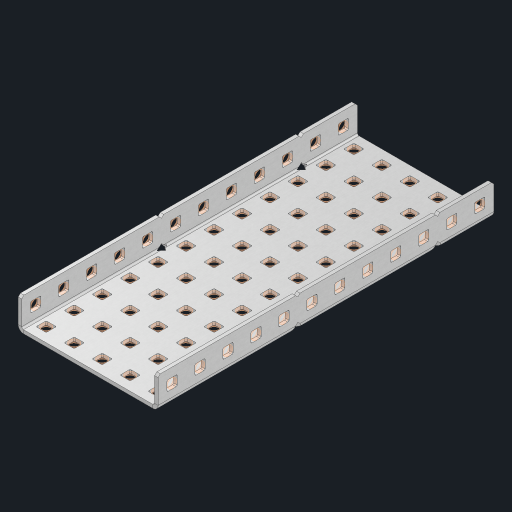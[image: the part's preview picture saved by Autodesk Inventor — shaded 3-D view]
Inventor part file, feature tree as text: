
AUTODESK INVENTOR PART (.ipt)
format: ipt  version: 2023 (Build 270158000, 158)  size: 1,160,192 bytes
history: native  units: in
note: dims shown in document units (in); Inventor stores cm internally (conversion verified against a paired STEP export)
features: other x89, extrude x83, sheet_metal_op x10, sketch x8, mirror x1, pattern_linear x1, chamfer x1
ambient origin geometry x8: Origin, YZ Plane, XZ Plane, XY Plane, X Axis, Y Axis, Z Axis, Center Point
bodies: Solid1 (feature_tree), Body (feature_tree)
feature tree (193):
  other  "Flange Pattern Plane"
  sheet_metal_op  "Flange Pattern"
  sheet_metal_op  "Body Pattern"
  other  "Arc Length"
  mirror  "Notch Mirror"
  pattern_linear  "Notch Pattern"  Spacing1=0.25in  [1 undecoded]
  chamfer  "End Chamfer"
  extrude  "Half Cut"  Depth=0.0625in
  sketch  "Sketch1"  dims[d0=2.5in]
  other  "Plate1"
  sketch  "Sketch2"  dims[d1=6.0in]
  other  "Plate2"
  sheet_metal_op  "Bend1"
  sheet_metal_op  "Corner1"
  sketch  "Sketch3"  dims[d2=0.0625in]
  other  "Flange Pattern Sketch"
  sketch  "Sketch7"  dims[d3=0.0625in]
  other  "Srf1"
  other  "Srf2"
  sketch  "Sketch8"  dims[d4=0.0312in]
  sketch  "Sketch9"  dims[d5=0.125in]
  other  "Srf91"
  sheet_metal_op  "Body Pattern Sketch"
  other  "Srf92"
  sketch  "Sketch13"  dims[d6=0.0625in]
  sketch  "Sketch14"  dims[d7=0.5in d8=90.0deg d9=0.0312in d10=0.25in d11=0.0625in d12=0.0625in d16=0.182in d17=0.02in d18=0.0625in d19=0.0in d20=0.25in d21=0.25in d46=0.172in d47=1.0in d48=0.0in d49=0.182in d50=0.02in d51=0.25in d52=0.25in d53=0.0625in d54=0.0in d55=0.172in d56=1.0in d57=0.0in d60=4.7244in d62=0.5in d63=1.9685in d65=0.5in d85=0.1473in d86=0.1782in d88=0.04in d89=0.0625in d90=0.0in d91=0.04in d92=0.0491in d95=2.5in d96=0.04in d97=0.25in d98=45.0deg d101=0.0in d102=2.497in d131=2.5in d132=4.7244in d134=0.5in d139=0.5in]
  other  "Srf856"
  other  "Srf1310"
  other  "Srf1311"
  other  "Srf1312"
  other  "Srf1376"
  other  "Srf1377"
  other  "Srf1728"
  other  "Srf1755"
  other  "Srf1878"
  other  "Srf1879"
  other  "Srf1880"
  other  "Srf1881"
  other  "Srf1882"
  other  "Srf1883"
  other  "Srf1884"
  other  "Srf1885"
  other  "Srf1886"
  other  "Srf1887"
  other  "Srf1888"
  other  "Srf1889"
  other  "Srf1890"
  other  "Srf1891"
  other  "Srf1892"
  other  "Srf1893"
  other  "Srf1894"
  other  "Srf1895"
  other  "Srf1942"
  other  "Srf1943"
  other  "Srf1944"
  other  "Srf1945"
  other  "Srf1946"
  other  "Srf1947"
  other  "Srf1948"
  other  "Srf1949"
  other  "Srf1950"
  other  "Srf1951"
  other  "Srf1952"
  other  "Srf1953"
  other  "Srf1954"
  other  "Srf1955"
  other  "Srf1956"
  other  "Srf1957"
  other  "Srf1958"
  other  "Srf1959"
  other  "Srf1960"
  other  "Srf1961"
  other  "Srf1962"
  other  "Srf1963"
  other  "Srf1964"
  other  "Srf1965"
  other  "Srf1966"
  other  "Srf1967"
  other  "Srf1968"
  other  "Srf1969"
  other  "Srf1970"
  other  "Srf2146"
  other  "Srf2147"
  other  "Srf2148"
  other  "Srf2149"
  other  "Srf2150"
  other  "Srf2151"
  other  "Srf2152"
  other  "Srf2153"
  other  "Srf2154"
  other  "Srf2155"
  other  "Srf2156"
  other  "Srf2157"
  other  "Srf2158"
  other  "Srf2159"
  other  "Srf2160"
  other  "Srf2161"
  other  "Srf2162"
  other  "Srf2163"
  other  "Srf2164"
  other  "Srf2165"
  other  "Srf2166"
  other  "Srf2167"
  other  "Srf2168"
  other  "Srf2169"
  other  "Srf2170"
  sheet_metal_op  "Flange Stamp"
  sheet_metal_op  "Flange Circle"
  sheet_metal_op  "Body Stamp"
  sheet_metal_op  "Body Circle"
  sheet_metal_op  "Notch"
  extrude  "ExtrusionSrf2"  Depth=0.0625in
  extrude  "ExtrusionSrf92"  Depth=2.5in
  extrude  "ExtrusionSrf856"  Depth=0.02in
  extrude  "ExtrusionSrf1310"  Depth=0.0625in
  extrude  "ExtrusionSrf1311"  TaperAngle=0.0deg  [1 undecoded]
  extrude  "ExtrusionSrf1312"  Depth=0.25in
  extrude  "ExtrusionSrf1376"  Depth=0.25in
  extrude  "ExtrusionSrf1377"  Depth=2.5in
  extrude  "ExtrusionSrf1728"  Depth=2.5in TaperAngle=0.0deg
  extrude  "ExtrusionSrf1755"  Depth=2.5in
  extrude  "ExtrusionSrf1878"  Depth=0.02in
  extrude  "ExtrusionSrf1879"  Depth=0.25in
  extrude  "ExtrusionSrf1880"  Depth=0.25in
  extrude  "ExtrusionSrf1881"  Depth=0.0625in
  extrude  "ExtrusionSrf1882"  TaperAngle=0.0deg  [1 undecoded]
  extrude  "ExtrusionSrf1883"  Depth=2.5in
  extrude  "ExtrusionSrf1884"  Depth=2.5in TaperAngle=0.0deg
  extrude  "ExtrusionSrf1885"  Depth=2.5in
  extrude  "ExtrusionSrf1886"  Depth=2.5in
  extrude  "ExtrusionSrf1887"  Depth=2.5in
  extrude  "ExtrusionSrf1888"  Depth=2.5in
  extrude  "ExtrusionSrf1889"  Depth=2.5in
  extrude  "ExtrusionSrf1890"  Depth=0.0625in
  extrude  "ExtrusionSrf1891"  TaperAngle=0.0deg  [1 undecoded]
  extrude  "ExtrusionSrf1892"  Depth=2.5in
  extrude  "ExtrusionSrf1893"  Depth=2.5in
  extrude  "ExtrusionSrf1894"  Depth=2.5in
  extrude  "ExtrusionSrf1895"  Depth=0.25in TaperAngle=45.0deg
  extrude  "ExtrusionSrf1942"  TaperAngle=0.0deg  [1 undecoded]
  extrude  "ExtrusionSrf1943"  Depth=2.5in
  extrude  "ExtrusionSrf1944"  Depth=2.5in
  extrude  "ExtrusionSrf1945"  Depth=2.5in
  extrude  "ExtrusionSrf1946"  Depth=2.5in
  extrude  "ExtrusionSrf1947"  Depth=2.5in
  extrude  "ExtrusionSrf1948"  [1 undecoded]
  extrude  "ExtrusionSrf1949"  [1 undecoded]
  extrude  "ExtrusionSrf1950"  [1 undecoded]
  extrude  "ExtrusionSrf1951"  [1 undecoded]
  extrude  "ExtrusionSrf1952"  [1 undecoded]
  extrude  "ExtrusionSrf1953"  [1 undecoded]
  extrude  "ExtrusionSrf1954"  [1 undecoded]
  extrude  "ExtrusionSrf1955"  [1 undecoded]
  extrude  "ExtrusionSrf1956"  [1 undecoded]
  extrude  "ExtrusionSrf1957"  [1 undecoded]
  extrude  "ExtrusionSrf1958"  [1 undecoded]
  extrude  "ExtrusionSrf1959"  [1 undecoded]
  extrude  "ExtrusionSrf1960"  [1 undecoded]
  extrude  "ExtrusionSrf1961"  [1 undecoded]
  extrude  "ExtrusionSrf1962"  [1 undecoded]
  extrude  "ExtrusionSrf1963"  [1 undecoded]
  extrude  "ExtrusionSrf1964"  [1 undecoded]
  extrude  "ExtrusionSrf1965"  [1 undecoded]
  extrude  "ExtrusionSrf1966"  [1 undecoded]
  extrude  "ExtrusionSrf1967"  [1 undecoded]
  extrude  "ExtrusionSrf1968"  [1 undecoded]
  extrude  "ExtrusionSrf1969"  [1 undecoded]
  extrude  "ExtrusionSrf1970"  [1 undecoded]
  extrude  "ExtrusionSrf2146"  [1 undecoded]
  extrude  "ExtrusionSrf2147"  [1 undecoded]
  extrude  "ExtrusionSrf2148"  [1 undecoded]
  extrude  "ExtrusionSrf2149"  [1 undecoded]
  extrude  "ExtrusionSrf2150"  [1 undecoded]
  extrude  "ExtrusionSrf2151"  [1 undecoded]
  extrude  "ExtrusionSrf2152"  [1 undecoded]
  extrude  "ExtrusionSrf2153"  [1 undecoded]
  extrude  "ExtrusionSrf2154"  [1 undecoded]
  extrude  "ExtrusionSrf2155"  [1 undecoded]
  extrude  "ExtrusionSrf2156"  [1 undecoded]
  extrude  "ExtrusionSrf2157"  [1 undecoded]
  extrude  "ExtrusionSrf2158"  [1 undecoded]
  extrude  "ExtrusionSrf2159"  [1 undecoded]
  extrude  "ExtrusionSrf2160"  [1 undecoded]
  extrude  "ExtrusionSrf2161"  [1 undecoded]
  extrude  "ExtrusionSrf2162"  [1 undecoded]
  extrude  "ExtrusionSrf2163"  [1 undecoded]
  extrude  "ExtrusionSrf2164"  [1 undecoded]
  extrude  "ExtrusionSrf2165"  [1 undecoded]
  extrude  "ExtrusionSrf2166"  [1 undecoded]
  extrude  "ExtrusionSrf2167"  [1 undecoded]
  extrude  "ExtrusionSrf2168"  [1 undecoded]
  extrude  "ExtrusionSrf2169"  [1 undecoded]
  extrude  "ExtrusionSrf2170"  [1 undecoded]
note: 53 required parameter values undecoded (feature->parameter linkage not recoverable at this tier; creation-order binding heuristic only, values carry confidence <= 0.55)
